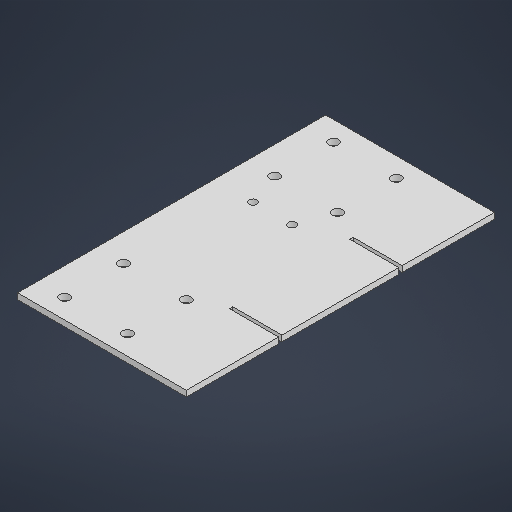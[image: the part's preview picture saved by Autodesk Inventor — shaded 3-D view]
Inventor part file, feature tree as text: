
AUTODESK INVENTOR PART (.ipt)
format: ipt  version: 2025.1 (Build 291241000, 241)  size: 194,048 bytes
history: native  units: mm
features: other x3, sketch x1
ambient origin geometry x8: Origin, YZ Plane, XZ Plane, XY Plane, X Axis, Y Axis, Z Axis, Center Point
bodies: Solid1 (feature_tree)
feature tree (4):
  other  "X Axis Base Plate Accurate.ipt"
  other  "Solid1::X Axis Base Plate Accurate.ipt"
  other  "TaggingFeature1"
  sketch  "Sketch1"  dims[d0=10.0mm]
